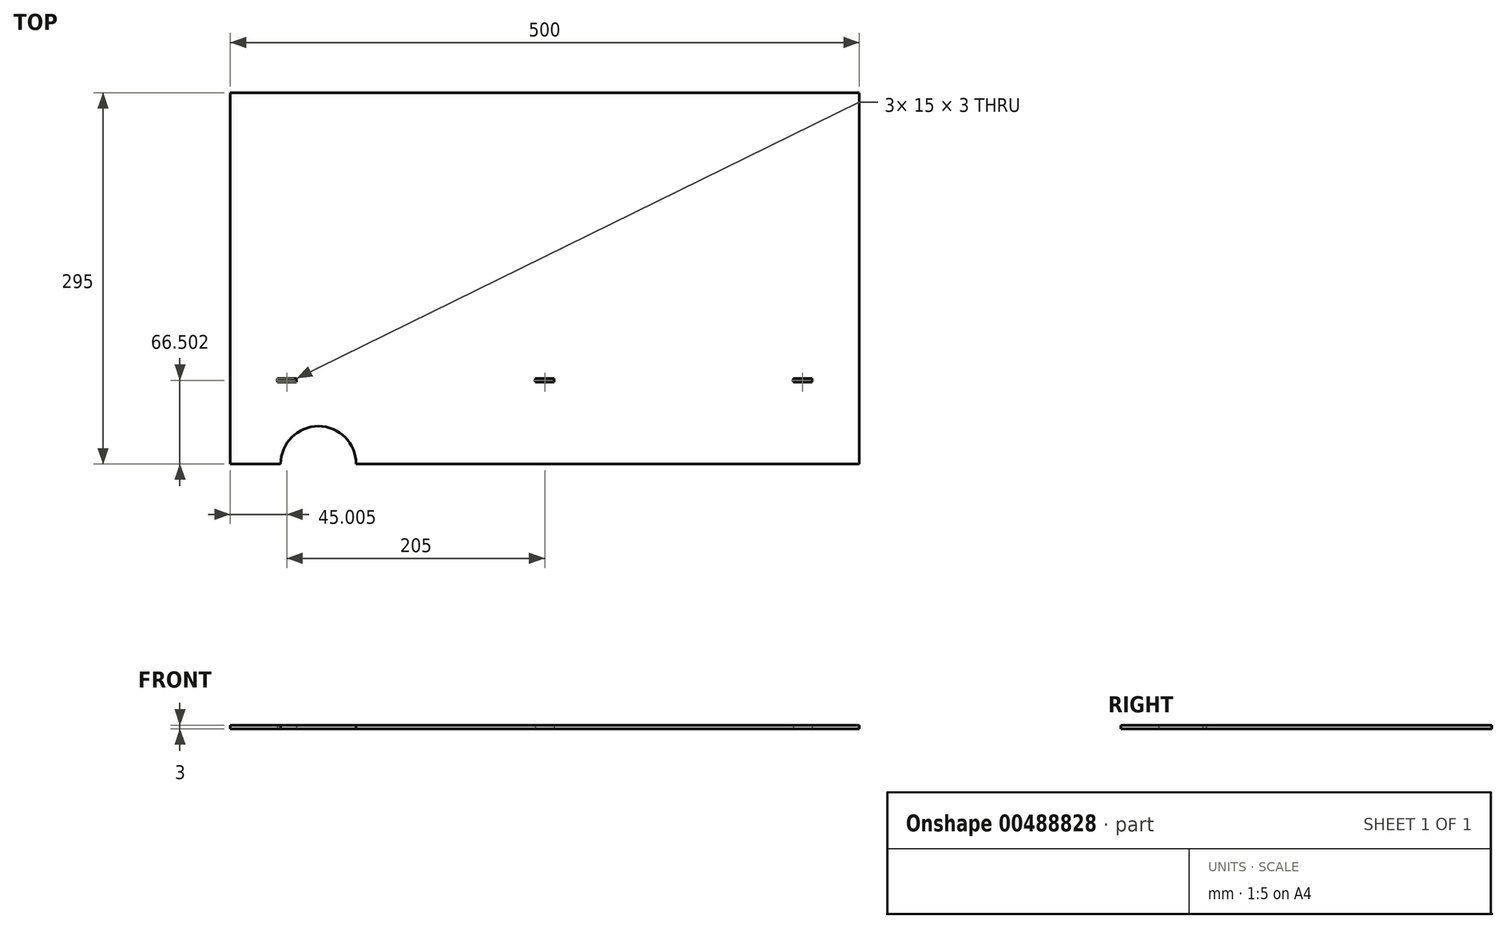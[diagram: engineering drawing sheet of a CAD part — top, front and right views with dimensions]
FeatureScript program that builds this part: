
annotation { "Feature Type Name" : "Feature", "Feature Type Description" : "" }
export const myFeature = defineFeature(function(context is Context, id is Id, definition is map)
    precondition{}
    {
        {
            var Q0;
            Q0=qCreatedBy(makeId("Top.planeOp"),FACE);
            var sketch = newSketch(context, id + "F0", { "sketchPlane" : qUnion([Q0])});
            skLineSegment(sketch, "E0.bottom", {"start": v(-225.66, 191.81) * mm, "end": v(274.34, 191.81) * mm});
            skLineSegment(sketch, "E0.top", {"start": v(-225.66, -103.19) * mm, "end": v(274.34, -103.19) * mm});
            skLineSegment(sketch, "E0.left", {"start": v(-225.66, 191.81) * mm, "end": v(-225.66, -103.19) * mm});
            skLineSegment(sketch, "E0.right", {"start": v(274.34, 191.81) * mm, "end": v(274.34, -103.19) * mm});
            skArc(sketch, "E1", {"start": v(-125.66, -103.19) * mm, "mid": v(-155.66, -73.19) * mm, "end": v(-185.66, -103.19) * mm});
            skLineSegment(sketch, "E2.bottom", {"start": v(-188.16, -35.19) * mm, "end": v(-173.16, -35.19) * mm});
            skLineSegment(sketch, "E2.top", {"start": v(-188.16, -38.19) * mm, "end": v(-173.16, -38.19) * mm});
            skLineSegment(sketch, "E2.left", {"start": v(-188.16, -35.19) * mm, "end": v(-188.16, -38.19) * mm});
            skLineSegment(sketch, "E2.right", {"start": v(236.84, -35.19) * mm, "end": v(236.84, -38.19) * mm});
            skPoint(sketch, "E3.oppositeSnap0", {"position": v(236.84, -36.69) * mm});
            skLineSegment(sketch, "E3.left", {"start": v(236.84, -36.69) * mm, "end": v(236.84, -36.69) * mm});
            skPoint(sketch, "E4.oppositeSnap0", {"position": v(-188.16, -36.69) * mm});
            skLineSegment(sketch, "E4.left", {"start": v(-188.16, -36.69) * mm, "end": v(-188.16, -36.69) * mm});
            skLineSegment(sketch, "E4.right", {"start": v(-225.66, -36.69) * mm, "end": v(-225.66, -36.69) * mm});
            skLineSegment(sketch, "E5.left", {"start": v(236.84, -31.85) * mm, "end": v(236.84, -32.08) * mm});
            skLineSegment(sketch, "E5.right", {"start": v(274.34, -45.72) * mm, "end": v(274.34, -45.95) * mm});
            skLineSegment(sketch, "E6.right", {"start": v(-173.16, -35.19) * mm, "end": v(-173.16, -38.19) * mm});
            skLineSegment(sketch, "E7.bottom", {"start": v(16.84, -35.19) * mm, "end": v(31.84, -35.19) * mm});
            skLineSegment(sketch, "E7.top", {"start": v(16.84, -38.19) * mm, "end": v(31.84, -38.19) * mm});
            skLineSegment(sketch, "E7.left", {"start": v(16.84, -35.19) * mm, "end": v(16.84, -38.19) * mm});
            skLineSegment(sketch, "E7.right", {"start": v(31.84, -35.19) * mm, "end": v(31.84, -38.19) * mm});
            skLineSegment(sketch, "E8.bottom", {"start": v(236.84, -35.19) * mm, "end": v(221.84, -35.19) * mm});
            skLineSegment(sketch, "E8.top", {"start": v(236.84, -38.19) * mm, "end": v(221.84, -38.19) * mm});
            skLineSegment(sketch, "E8.right", {"start": v(221.84, -35.19) * mm, "end": v(221.84, -38.19) * mm});
            skLineSegment(sketch, "E9.trimOffspring", {"start": v(221.84, -35.19) * mm, "end": v(236.84, -35.19) * mm});
            skLineSegment(sketch, "E10.trimOffspring", {"start": v(221.84, -38.19) * mm, "end": v(236.84, -38.19) * mm});
            skSolve(sketch);
        }
        {
            var Q0;
            Q0=makeQuery(id+"F0.imprint","IMPRINT",FACE,{"disambiguationData":[TD([[makeQuery(id+"F0.imprint","IMPRINT",EDGE,{"derivedFrom":sQuery(id+"F0.wireOp",EDGE,"E0.bottom")}),-1.0]])]});
            extrude(context, id + "F1", {"entities" : qUnion([Q0]), "depth" : 3 * mm});
        }
        {
            var Q0;
            Q0 = qSketchRegion(id + "F0", true);
            extrude(context, id + "F2", {"entities" : qUnion([Q0]), "operationType" : NewBodyOperationType.REMOVE, "oppositeDirection" : true, "depth" : 25 * mm, "offsetDistance" : 25 * mm});
        }
    });
